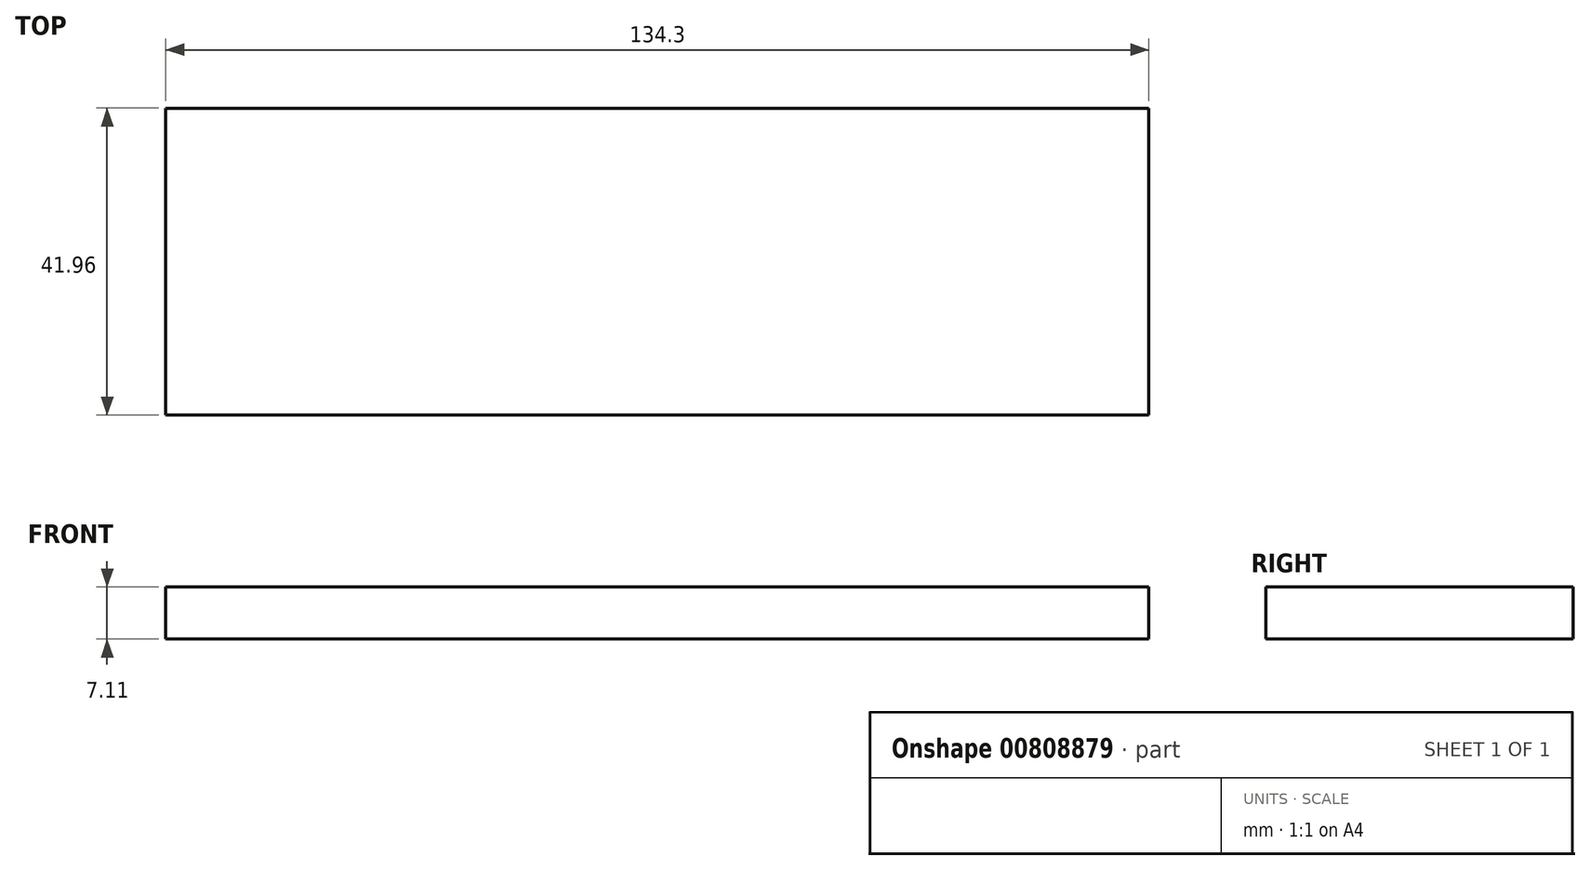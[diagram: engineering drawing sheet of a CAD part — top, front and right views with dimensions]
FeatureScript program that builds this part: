
annotation { "Feature Type Name" : "Feature", "Feature Type Description" : "" }
export const myFeature = defineFeature(function(context is Context, id is Id, definition is map)
    precondition{}
    {
        {
            var Q0;
            Q0=qCreatedBy(makeId("Top.planeOp"),FACE);
            var sketch = newSketch(context, id + "F0", { "sketchPlane" : qUnion([Q0])});
            skLineSegment(sketch, "E0.bottom", {"start": v(-67.15, 20.98) * mm, "end": v(67.15, 20.98) * mm});
            skLineSegment(sketch, "E0.top", {"start": v(-67.15, -20.98) * mm, "end": v(67.15, -20.98) * mm});
            skLineSegment(sketch, "E0.left", {"start": v(-67.15, 20.98) * mm, "end": v(-67.15, -20.98) * mm});
            skLineSegment(sketch, "E0.right", {"start": v(67.15, 20.98) * mm, "end": v(67.15, -20.98) * mm});
            skPoint(sketch, "E0.middle", {"position": v(0, 0) * mm});
            skSolve(sketch);
        }
        {
            var Q0;
            Q0 = qSketchRegion(id + "F0", true);
            extrude(context, id + "F1", {"entities" : qUnion([Q0]), "depth" : 7.11 * mm, "offsetDistance" : 25.4 * mm});
        }
    });
